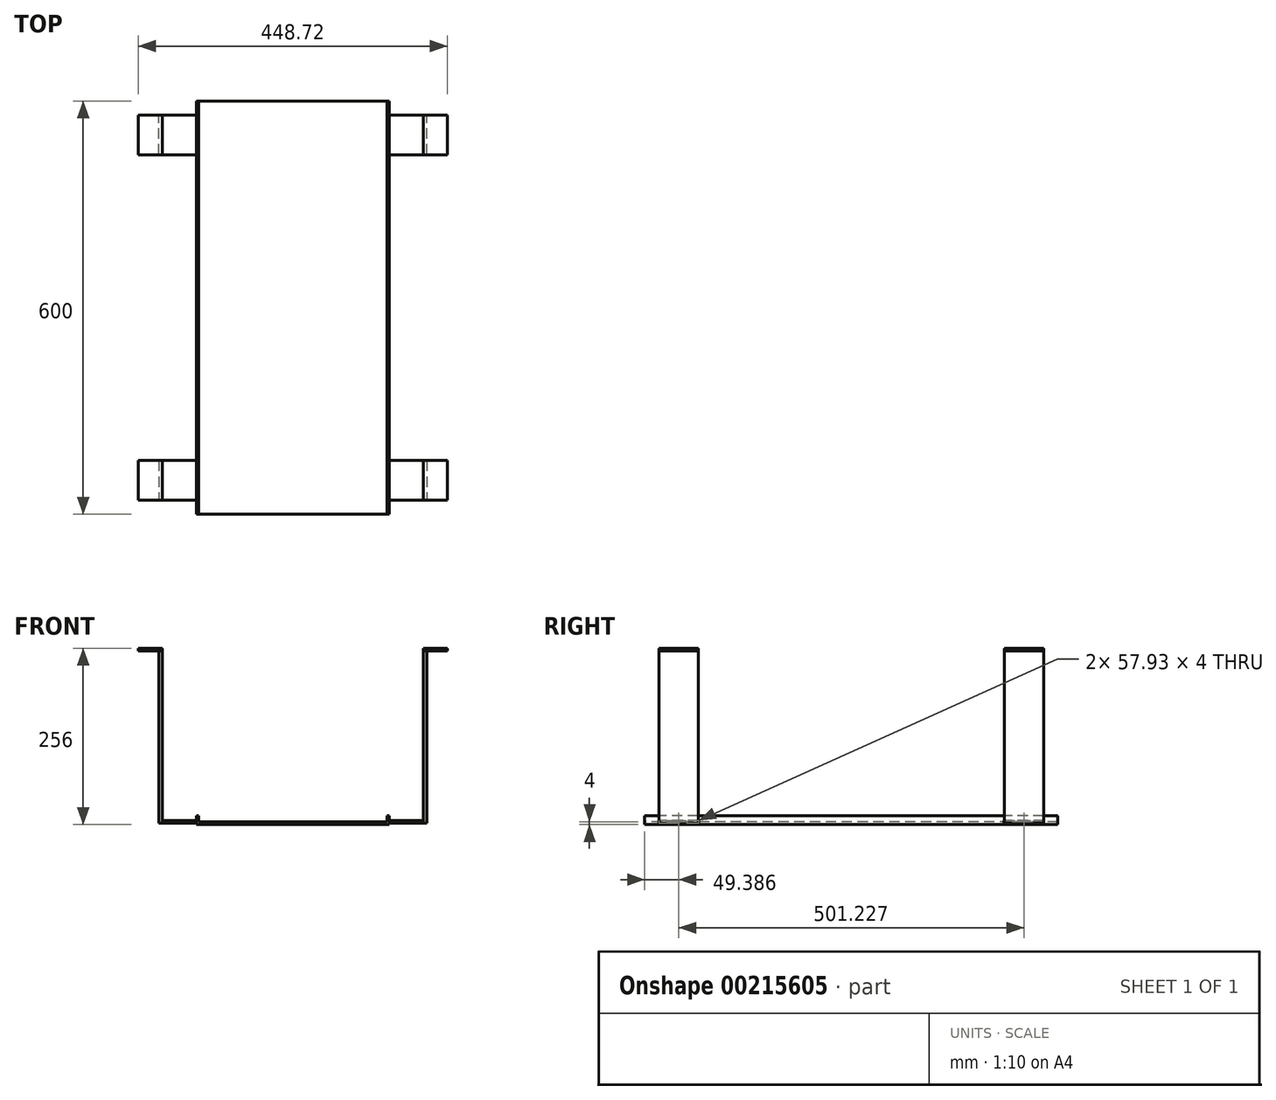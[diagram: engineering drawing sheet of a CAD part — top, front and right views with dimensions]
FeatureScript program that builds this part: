
annotation { "Feature Type Name" : "Feature", "Feature Type Description" : "" }
export const myFeature = defineFeature(function(context is Context, id is Id, definition is map)
    precondition{}
    {
        {
            var Q0;
            Q0=qCreatedBy(makeId("Top.planeOp"),FACE);
            var sketch = newSketch(context, id + "F0", { "sketchPlane" : qUnion([Q0])});
            skLineSegment(sketch, "E0.bottom", {"start": v(-140, 300) * mm, "end": v(140, 300) * mm});
            skLineSegment(sketch, "E0.top", {"start": v(-140, -300) * mm, "end": v(140, -300) * mm});
            skLineSegment(sketch, "E0.left", {"start": v(-140, 300) * mm, "end": v(-140, -300) * mm});
            skLineSegment(sketch, "E0.right", {"start": v(140, 300) * mm, "end": v(140, -300) * mm});
            skPoint(sketch, "E0.middle", {"position": v(0, 0) * mm});
            skSolve(sketch);
        }
        {
            var Q0;
            Q0 = qSketchRegion(id + "F0", true);
            extrude(context, id + "F1", {"entities" : qUnion([Q0]), "endBound" : BoundingType.SYMMETRIC, "depth" : 4 * mm});
        }
        {
            var Q0;
            Q0=makeQuery(id+"F1.opExtrude","CAP_FACE",FACE,{"disambiguationData":[OSD([sQuery(id+"F0.wireOp",EDGE,"E0.bottom"),sQuery(id+"F0.wireOp",EDGE,"E0.top"),sQuery(id+"F0.wireOp",EDGE,"E0.left"),sQuery(id+"F0.wireOp",EDGE,"E0.right")])],"isStart":false});
            var sketch = newSketch(context, id + "F2", { "sketchPlane" : qUnion([Q0])});
            skLineSegment(sketch, "E1.0", {"start": v(-137, 300) * mm, "end": v(-137, -300) * mm});
            skLineSegment(sketch, "E2.0", {"start": v(137, 300) * mm, "end": v(137, -300) * mm});
            skLineSegment(sketch, "E3", {"start": v(-137, 300) * mm, "end": v(-140, 300) * mm});
            skLineSegment(sketch, "E4", {"start": v(-140, 300) * mm, "end": v(-140, -300) * mm});
            skLineSegment(sketch, "E5", {"start": v(-140, -300) * mm, "end": v(-137, -300) * mm});
            skLineSegment(sketch, "E6", {"start": v(137, -300) * mm, "end": v(140, -300) * mm});
            skLineSegment(sketch, "E7", {"start": v(140, -300) * mm, "end": v(140, 300) * mm});
            skLineSegment(sketch, "E8", {"start": v(140, 300) * mm, "end": v(137, 300) * mm});
            skSolve(sketch);
        }
        {
            var Q0;
            Q0 = qSketchRegion(id + "F2", true);
            extrude(context, id + "F3", {"entities" : qUnion([Q0]), "operationType" : NewBodyOperationType.ADD, "depth" : 9 * mm});
        }
        {
            var Q0;
            Q0=qCreatedBy(makeId("Top.planeOp"),FACE);
            var sketch = newSketch(context, id + "F4", { "sketchPlane" : qUnion([Q0])});
            skLineSegment(sketch, "E9.bottom", {"start": v(-139.81, 279.58) * mm, "end": v(-189.81, 279.58) * mm});
            skLineSegment(sketch, "E9.top", {"start": v(-139.81, 221.65) * mm, "end": v(-189.81, 221.65) * mm});
            skLineSegment(sketch, "E9.left", {"start": v(-139.81, 279.58) * mm, "end": v(-139.81, 221.65) * mm});
            skLineSegment(sketch, "E9.right", {"start": v(-189.81, 279.58) * mm, "end": v(-189.81, 221.65) * mm});
            skLineSegment(sketch, "E10.MirrorCS", {"start": v(139.81, 221.65) * mm, "end": v(189.81, 221.65) * mm});
            skLineSegment(sketch, "E11.MirrorCS", {"start": v(189.81, 279.58) * mm, "end": v(189.81, 221.65) * mm});
            skLineSegment(sketch, "E12.MirrorCS", {"start": v(139.81, 279.58) * mm, "end": v(189.81, 279.58) * mm});
            skLineSegment(sketch, "E13.MirrorCS", {"start": v(139.81, 279.58) * mm, "end": v(139.81, 221.65) * mm});
            skLineSegment(sketch, "E14.MirrorCS", {"start": v(-189.81, -279.58) * mm, "end": v(-189.81, -221.65) * mm});
            skLineSegment(sketch, "E15.MirrorCS", {"start": v(-139.81, -221.65) * mm, "end": v(-189.81, -221.65) * mm});
            skLineSegment(sketch, "E16.MirrorCS", {"start": v(-139.81, -279.58) * mm, "end": v(-189.81, -279.58) * mm});
            skLineSegment(sketch, "E17.MirrorCS", {"start": v(-139.81, -279.58) * mm, "end": v(-139.81, -221.65) * mm});
            skLineSegment(sketch, "E18.MirrorCS", {"start": v(139.81, -279.58) * mm, "end": v(189.81, -279.58) * mm});
            skLineSegment(sketch, "E19.MirrorCS", {"start": v(139.81, -221.65) * mm, "end": v(189.81, -221.65) * mm});
            skLineSegment(sketch, "E20.MirrorCS", {"start": v(189.81, -279.58) * mm, "end": v(189.81, -221.65) * mm});
            skLineSegment(sketch, "E21", {"start": v(139.81, -221.65) * mm, "end": v(139.81, -279.58) * mm});
            skSolve(sketch);
        }
        {
            var Q0;
            Q0 = qSketchRegion(id + "F4", true);
            extrude(context, id + "F5", {"entities" : qUnion([Q0]), "operationType" : NewBodyOperationType.ADD, "depth" : 4 * mm});
        }
        {
            var Q0;
            Q0=qCreatedBy(makeId("Top.planeOp"),FACE);
            var sketch = newSketch(context, id + "F6", { "sketchPlane" : qUnion([Q0])});
            skLineSegment(sketch, "E22", {"start": v(-189.36, 279.47) * mm, "end": v(-189.36, 222.5) * mm});
            skLineSegment(sketch, "E23", {"start": v(-194.6, 222.5) * mm, "end": v(-194.6, 279.44) * mm});
            skLineSegment(sketch, "E24", {"start": v(-194.6, 279.44) * mm, "end": v(-189.36, 279.47) * mm});
            skLineSegment(sketch, "E25.MirrorCS", {"start": v(-194.6, -279.44) * mm, "end": v(-189.36, -279.47) * mm});
            skLineSegment(sketch, "E26.MirrorCS", {"start": v(-189.36, -222.5) * mm, "end": v(-194.6, -222.5) * mm});
            skLineSegment(sketch, "E27.MirrorCS", {"start": v(-189.36, -279.47) * mm, "end": v(-189.36, -222.5) * mm});
            skLineSegment(sketch, "E28.MirrorCS", {"start": v(-194.6, -222.5) * mm, "end": v(-194.6, -279.44) * mm});
            skLineSegment(sketch, "E29.MirrorCS", {"start": v(194.6, 279.44) * mm, "end": v(189.36, 279.47) * mm});
            skLineSegment(sketch, "E30.MirrorCS", {"start": v(189.36, 222.5) * mm, "end": v(194.6, 222.5) * mm});
            skLineSegment(sketch, "E31.MirrorCS", {"start": v(194.6, 222.5) * mm, "end": v(194.6, 279.44) * mm});
            skLineSegment(sketch, "E32.MirrorCS", {"start": v(189.36, 279.47) * mm, "end": v(189.36, 222.5) * mm});
            skLineSegment(sketch, "E33.MirrorCS", {"start": v(189.36, -222.5) * mm, "end": v(194.6, -222.5) * mm});
            skLineSegment(sketch, "E34.MirrorCS", {"start": v(194.6, -279.44) * mm, "end": v(189.36, -279.47) * mm});
            skLineSegment(sketch, "E35.MirrorCS", {"start": v(194.6, -222.5) * mm, "end": v(194.6, -279.44) * mm});
            skLineSegment(sketch, "E36.MirrorCS", {"start": v(189.36, -279.47) * mm, "end": v(189.36, -222.5) * mm});
            skLineSegment(sketch, "E37", {"start": v(-189.36, 222.5) * mm, "end": v(-194.6, 222.5) * mm});
            skPoint(sketch, "E38.orphan", {"position": v(-194.6, 222.5) * mm});
            skPoint(sketch, "E39.orphan", {"position": v(-189.36, 222.5) * mm});
            skPoint(sketch, "E40.orphan", {"position": v(-184.36, 222.5) * mm});
            skSolve(sketch);
        }
        {
            var Q0;
            Q0=makeQuery(id+"F6.imprint","IMPRINT",FACE,{"disambiguationData":[TD([[makeQuery(id+"F6.imprint","IMPRINT",EDGE,{"derivedFrom":sQuery(id+"F6.wireOp",EDGE,"E22")}),-1.0]])]});
            var Q1;
            Q1=makeQuery(id+"F6.imprint","IMPRINT",FACE,{"disambiguationData":[TD([[makeQuery(id+"F6.imprint","IMPRINT",EDGE,{"derivedFrom":sQuery(id+"F6.wireOp",EDGE,"E29.MirrorCS")}),1.0]])]});
            var Q2;
            Q2=makeQuery(id+"F6.imprint","IMPRINT",FACE,{"disambiguationData":[TD([[makeQuery(id+"F6.imprint","IMPRINT",EDGE,{"derivedFrom":sQuery(id+"F6.wireOp",EDGE,"E33.MirrorCS")}),-1.0]])]});
            var Q3;
            Q3=makeQuery(id+"F6.imprint","IMPRINT",FACE,{"disambiguationData":[TD([[makeQuery(id+"F6.imprint","IMPRINT",EDGE,{"derivedFrom":sQuery(id+"F6.wireOp",EDGE,"E25.MirrorCS")}),1.0]])]});
            extrude(context, id + "F7", {"entities" : qUnion([Q0, Q1, Q2, Q3]), "operationType" : NewBodyOperationType.ADD, "depth" : 250 * mm});
        }
        {
            var Q0;
            Q0=makeQuery(id+"F7.opExtrude","CAP_FACE",FACE,{"disambiguationData":[OSD([sQuery(id+"F6.wireOp",EDGE,"E22"),sQuery(id+"F6.wireOp",EDGE,"77NqpvgX-ehrn-EI3z-IrPZ-t6DXSWd2carS"),sQuery(id+"F6.wireOp",EDGE,"E23"),sQuery(id+"F6.wireOp",EDGE,"E24")])],"isStart":false});
            var sketch = newSketch(context, id + "F8", { "sketchPlane" : qUnion([Q0])});
            skLineSegment(sketch, "E41.bottom", {"start": v(-189.36, 279.47) * mm, "end": v(-224.36, 279.47) * mm});
            skLineSegment(sketch, "E41.top", {"start": v(-189.36, 222.04) * mm, "end": v(-224.36, 222.04) * mm});
            skLineSegment(sketch, "E41.left", {"start": v(-189.36, 279.47) * mm, "end": v(-189.36, 222.04) * mm});
            skLineSegment(sketch, "E41.right", {"start": v(-224.36, 279.47) * mm, "end": v(-224.36, 222.04) * mm});
            skLineSegment(sketch, "E42.MirrorCS", {"start": v(224.36, 279.47) * mm, "end": v(224.36, 222.04) * mm});
            skLineSegment(sketch, "E43.MirrorCS", {"start": v(189.36, 279.47) * mm, "end": v(189.36, 222.04) * mm});
            skLineSegment(sketch, "E44.MirrorCS", {"start": v(189.36, 222.04) * mm, "end": v(224.36, 222.04) * mm});
            skLineSegment(sketch, "E45.MirrorCS", {"start": v(189.36, 279.47) * mm, "end": v(224.36, 279.47) * mm});
            skLineSegment(sketch, "E46.MirrorCS", {"start": v(189.36, -279.47) * mm, "end": v(224.36, -279.47) * mm});
            skLineSegment(sketch, "E47.MirrorCS", {"start": v(189.36, -222.04) * mm, "end": v(224.36, -222.04) * mm});
            skLineSegment(sketch, "E48.MirrorCS", {"start": v(189.36, -279.47) * mm, "end": v(189.36, -222.04) * mm});
            skLineSegment(sketch, "E49.MirrorCS", {"start": v(224.36, -279.47) * mm, "end": v(224.36, -222.04) * mm});
            skLineSegment(sketch, "E50.MirrorCS", {"start": v(-224.36, -279.47) * mm, "end": v(-224.36, -222.04) * mm});
            skLineSegment(sketch, "E51.MirrorCS", {"start": v(-189.36, -279.47) * mm, "end": v(-224.36, -279.47) * mm});
            skLineSegment(sketch, "E52.MirrorCS", {"start": v(-189.36, -222.04) * mm, "end": v(-224.36, -222.04) * mm});
            skLineSegment(sketch, "E53.MirrorCS", {"start": v(-189.36, -279.47) * mm, "end": v(-189.36, -222.04) * mm});
            skSolve(sketch);
        }
        {
            var Q0;
            Q0 = qSketchRegion(id + "F8", true);
            extrude(context, id + "F9", {"entities" : qUnion([Q0]), "operationType" : NewBodyOperationType.ADD, "depth" : 4 * mm});
        }
    });
